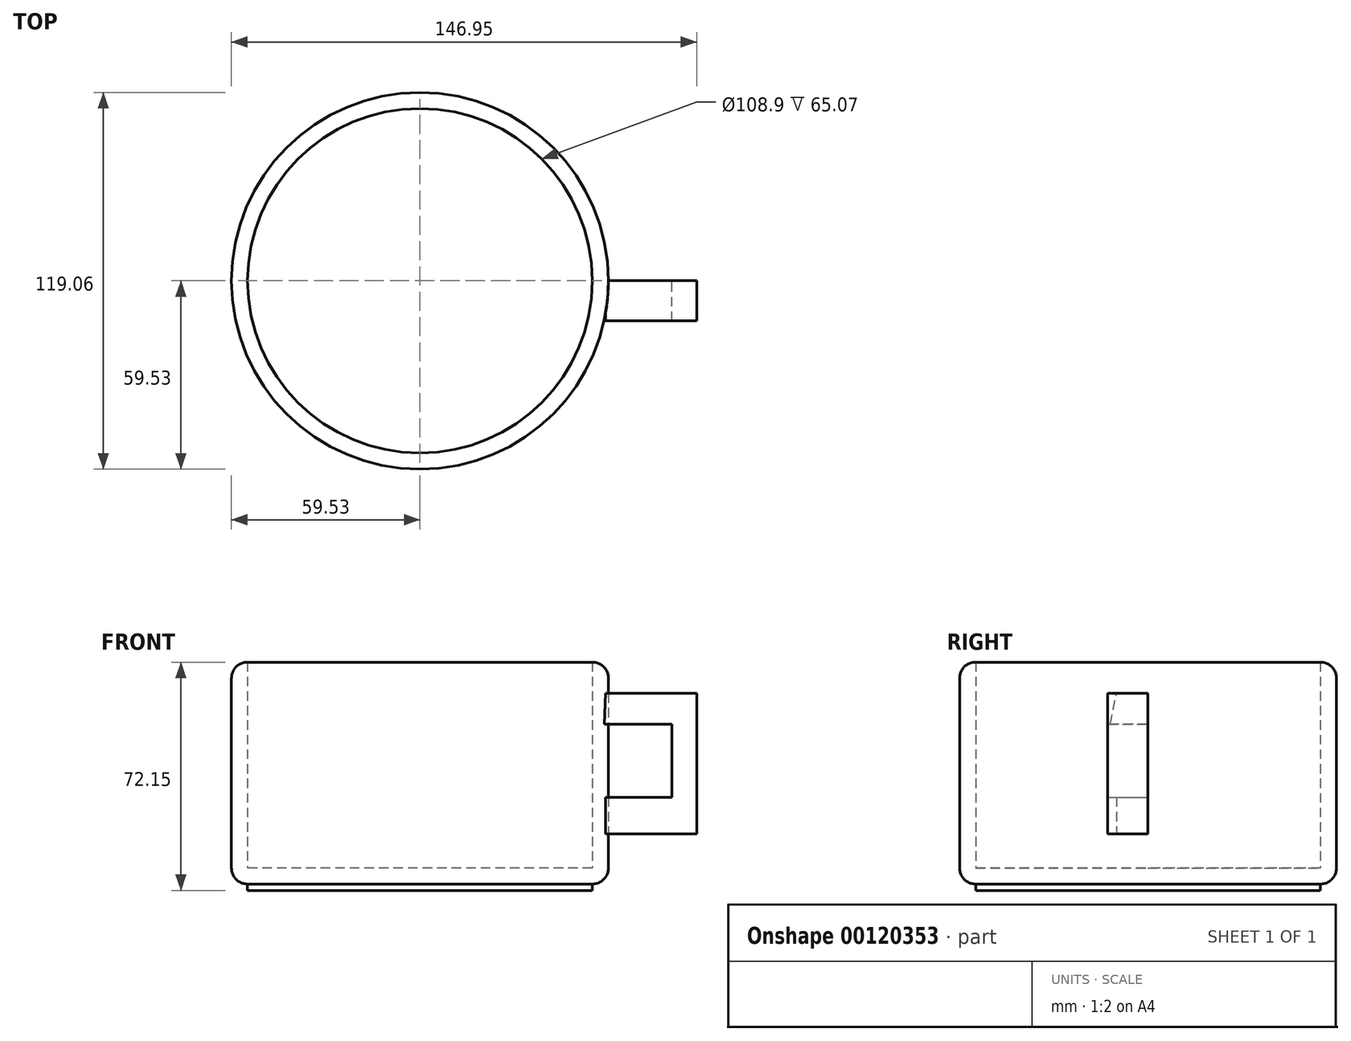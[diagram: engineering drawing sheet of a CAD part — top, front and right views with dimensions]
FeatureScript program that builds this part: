
annotation { "Feature Type Name" : "Feature", "Feature Type Description" : "" }
export const myFeature = defineFeature(function(context is Context, id is Id, definition is map)
    precondition{}
    {
        {
            var Q0;
            Q0=qCreatedBy(makeId("Top.planeOp"),FACE);
            var sketch = newSketch(context, id + "F0", { "sketchPlane" : qUnion([Q0])});
            skCircle(sketch, "E0", {"center": v(0, 0) * mm, "radius": 59.53 * mm});
            skCircle(sketch, "E1", {"center": v(0, 0) * mm, "radius": 55.27 * mm});
            skSolve(sketch);
        }
        {
            var Q0;
            Q0=makeQuery(id+"F0.imprint","IMPRINT",FACE,{"disambiguationData":[TD([[makeQuery(id+"F0.imprint","IMPRINT",EDGE,{"derivedFrom":sQuery(id+"F0.wireOp",EDGE,"E0")}),1.0]])]});
            var Q1;
            Q1=makeQuery(id+"F0.imprint","IMPRINT",FACE,{"disambiguationData":[TD([[makeQuery(id+"F0.imprint","IMPRINT",EDGE,{"derivedFrom":sQuery(id+"F0.wireOp",EDGE,"E1")}),1.0]])]});
            extrude(context, id + "F1", {"entities" : qUnion([Q0, Q1]), "depth" : 70.15 * mm});
        }
        {
            var Q0;
            Q0=makeQuery(id+"F1.opExtrude","CAP_FACE",FACE,{"disambiguationData":[OSD([sQuery(id+"F0.wireOp",EDGE,"E0")])],"isStart":false});
            shell(context, id + "F2", {"entities" : qUnion([Q0]), "thickness" : 5.08 * mm});
        }
        {
            var Q0;
            Q0=qCreatedBy(makeId("Front.planeOp"),FACE);
            var sketch = newSketch(context, id + "F3", { "sketchPlane" : qUnion([Q0])});
            skLineSegment(sketch, "E2", {"start": v(58.7, 60.28) * mm, "end": v(87.42, 60.28) * mm});
            skLineSegment(sketch, "E3", {"start": v(87.42, 60.28) * mm, "end": v(87.42, 15.9) * mm});
            skLineSegment(sketch, "E4", {"start": v(87.42, 15.9) * mm, "end": v(58.7, 15.9) * mm});
            skLineSegment(sketch, "E5", {"start": v(58.7, 15.9) * mm, "end": v(58.7, 27.45) * mm});
            skLineSegment(sketch, "E6", {"start": v(58.7, 27.45) * mm, "end": v(79.59, 27.45) * mm});
            skLineSegment(sketch, "E7", {"start": v(79.59, 27.45) * mm, "end": v(79.59, 50.58) * mm});
            skLineSegment(sketch, "E8", {"start": v(79.59, 50.58) * mm, "end": v(58.33, 50.58) * mm});
            skLineSegment(sketch, "E9", {"start": v(58.33, 50.58) * mm, "end": v(58.7, 60.28) * mm});
            skSolve(sketch);
        }
        {
            var Q0;
            Q0=makeQuery(id+"F3.imprint","IMPRINT",FACE,{"disambiguationData":[TD([[makeQuery(id+"F3.imprint","IMPRINT",EDGE,{"derivedFrom":sQuery(id+"F3.wireOp",EDGE,"E2")}),-1.0]])]});
            extrude(context, id + "F4", {"entities" : qUnion([Q0]), "operationType" : NewBodyOperationType.ADD, "depth" : 12.7 * mm});
        }
        {
            var Q0;
            Q0=makeQuery(id+"F1.opExtrude","CAP_EDGE",EDGE,{"disambiguationData":[OSD([sQuery(id+"F0.wireOp",EDGE,"E0")])],"isStart":false});
            fillet(context, id + "F5", {"entities" : qUnion([Q0]), "radius" : 5.08 * mm, "tangentPropagation" : true, "allowEdgeOverflow" : false});
        }
        {
            var Q0;
            Q0=makeQuery(id+"F1.opExtrude","CAP_EDGE",EDGE,{"disambiguationData":[OSD([sQuery(id+"F0.wireOp",EDGE,"E0")])],"isStart":true});
            fillet(context, id + "F6", {"entities" : qUnion([Q0]), "radius" : 5.08 * mm, "tangentPropagation" : true, "allowEdgeOverflow" : false});
        }
        {
            var Q0;
            Q0=makeQuery(id+"F1.opExtrude","CAP_FACE",FACE,{"disambiguationData":[OSD([sQuery(id+"F0.wireOp",EDGE,"E0")])],"isStart":true});
            extrude(context, id + "F7", {"entities" : qUnion([Q0]), "operationType" : NewBodyOperationType.ADD, "depth" : 2 * mm});
        }
    });
